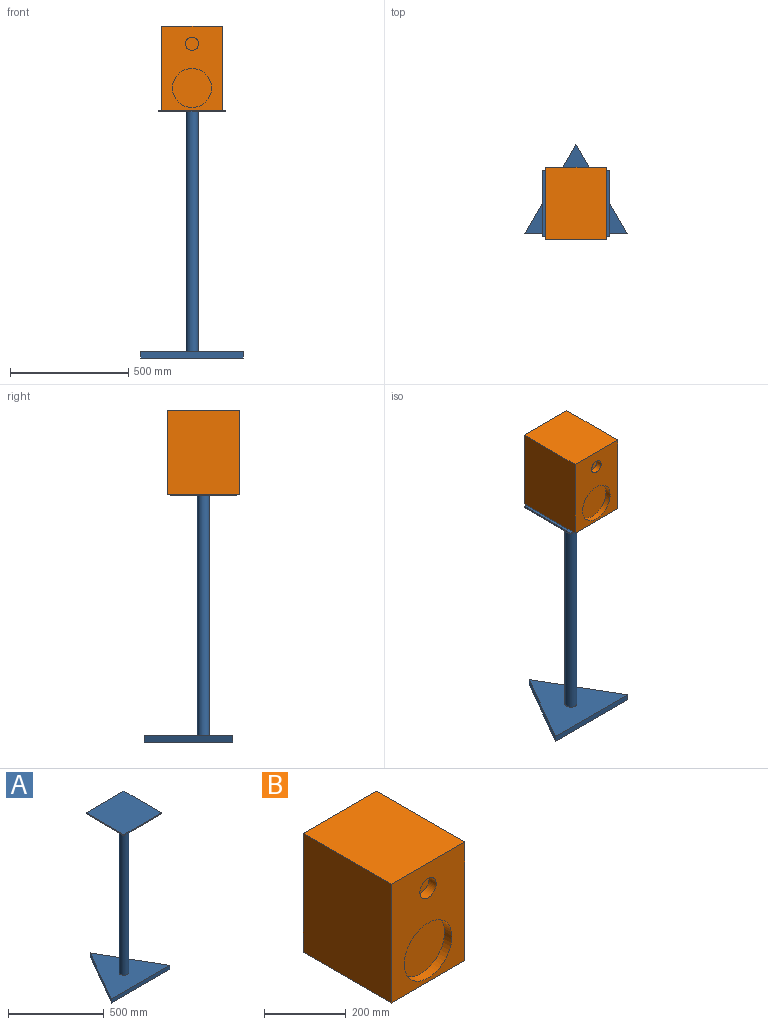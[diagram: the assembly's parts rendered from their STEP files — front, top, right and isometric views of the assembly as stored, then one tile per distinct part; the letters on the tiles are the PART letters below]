
ASSEMBLY  parts=2 mates=1
PART A: 12 faces, bbox 431.8x389x1047.8 mm
  f0: plane 373.95x215.9mm, normal (-0.87,0.5,0), area 10967.7mm2, adj f1,f2,f3,f4
  f1: plane 431.8x25.4mm, normal (0,-1,0), area 10967.7mm2, adj f0,f2,f3,f4
  f2: plane 373.95x215.9mm, normal (0.87,0.5,0), area 10967.7mm2, adj f0,f1,f3,f4
  f3: plane 431.8x373.95mm, normal (0,0,1), area 78708.9mm2, adj f0,f1,f2,f5
  f4: plane 431.8x373.95mm, normal (0,0,-1), area 80735.8mm2, adj f0,f1,f2
  f5: cylinder r=25.4mm len=1016mm, axis (0,0,-1), area 162146.4mm2, adj f3,f11
  f6: plane 279.4x6.35mm, normal (1,0,0), area 1774.2mm2, adj f7,f9,f10,f11
  f7: plane 279.4x6.35mm, normal (0,1,0), area 1774.2mm2, adj f6,f8,f10,f11
  f8: plane 279.4x6.35mm, normal (-1,0,0), area 1774.2mm2, adj f7,f9,f10,f11
  f9: plane 279.4x6.35mm, normal (0,-1,0), area 1774.2mm2, adj f6,f8,f10,f11
  f10: plane 279.4x279.4mm, normal (0,0,1), area 78064.4mm2, adj f6,f7,f8,f9
  f11: plane 279.4x279.4mm, normal (0,0,-1), area 76037.5mm2, adj f5,f6,f7,f8,f9
PART B: 10 faces, bbox 254x304.8x355.6 mm
  f0: plane 355.6x304.8mm, normal (-1,0,0), area 108386.9mm2, adj f1,f3,f4,f5
  f1: plane 304.8x254mm, normal (0,0,-1), area 77419.2mm2, adj f0,f2,f4,f5
  f2: plane 355.6x304.8mm, normal (1,0,0), area 108386.9mm2, adj f1,f3,f4,f5
  f3: plane 304.8x254mm, normal (0,0,1), area 77419.2mm2, adj f0,f2,f4,f5
  f4: plane 355.6x254mm, normal (0,-1,0), area 66483.4mm2, adj f0,f1,f2,f3,f6,f8
  f5: plane 355.6x254mm, normal (0,1,0), area 90322.4mm2, adj f0,f1,f2,f3
  f6: cylinder r=28.29mm len=56.58mm, axis (0,-1,0), area 4514.8mm2, adj f4,f7
  f7: plane 56.58x56.58mm, normal (0,-1,0), area 2514.2mm2, adj f6
  f8: cylinder r=82.39mm len=164.78mm, axis (0,-1,0), area 13148.7mm2, adj f4,f9
  f9: plane 164.78x164.78mm, normal (0,-1,0), area 21324.8mm2, adj f8
PLACE A t=(225.02,-1352.73,446.96)mm fixed
PLACE B t=(-1335.48,47.11,1494.71)mm
MATE fastened A.f5 <-> B.f1  axis (0,0,1) through (-1208.48,-105.29,1494.71)mm
